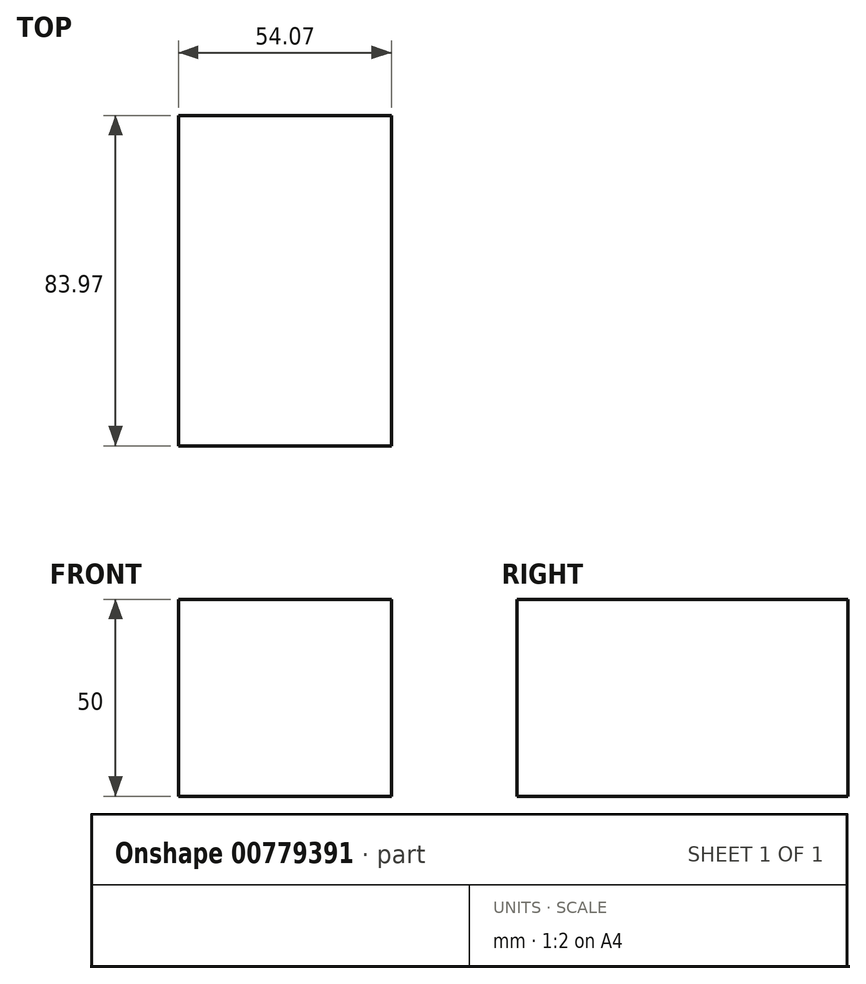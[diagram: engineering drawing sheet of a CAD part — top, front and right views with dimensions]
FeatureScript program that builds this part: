
annotation { "Feature Type Name" : "Feature", "Feature Type Description" : "" }
export const myFeature = defineFeature(function(context is Context, id is Id, definition is map)
    precondition{}
    {
        {
            var Q0;
            Q0=qCreatedBy(makeId("Top.planeOp"),FACE);
            var sketch = newSketch(context, id + "F0", { "sketchPlane" : qUnion([Q0])});
            skLineSegment(sketch, "E0.bottom", {"start": v(-58.53, -47.97) * mm, "end": v(-4.46, -47.97) * mm});
            skLineSegment(sketch, "E0.top", {"start": v(-58.53, 36) * mm, "end": v(-4.46, 36) * mm});
            skLineSegment(sketch, "E0.left", {"start": v(-58.53, -47.97) * mm, "end": v(-58.53, 36) * mm});
            skLineSegment(sketch, "E0.right", {"start": v(-4.46, -47.97) * mm, "end": v(-4.46, 36) * mm});
            skSolve(sketch);
        }
        {
            var Q0;
            Q0=makeQuery(id+"F0.imprint","IMPRINT",FACE,{"disambiguationData":[TD([[makeQuery(id+"F0.imprint","IMPRINT",EDGE,{"derivedFrom":sQuery(id+"F0.wireOp",EDGE,"E0.bottom")}),1.0]])]});
            extrude(context, id + "F1", {"entities" : qUnion([Q0]), "depth" : 50 * mm, "offsetDistance" : 25.4 * mm});
        }
    });
